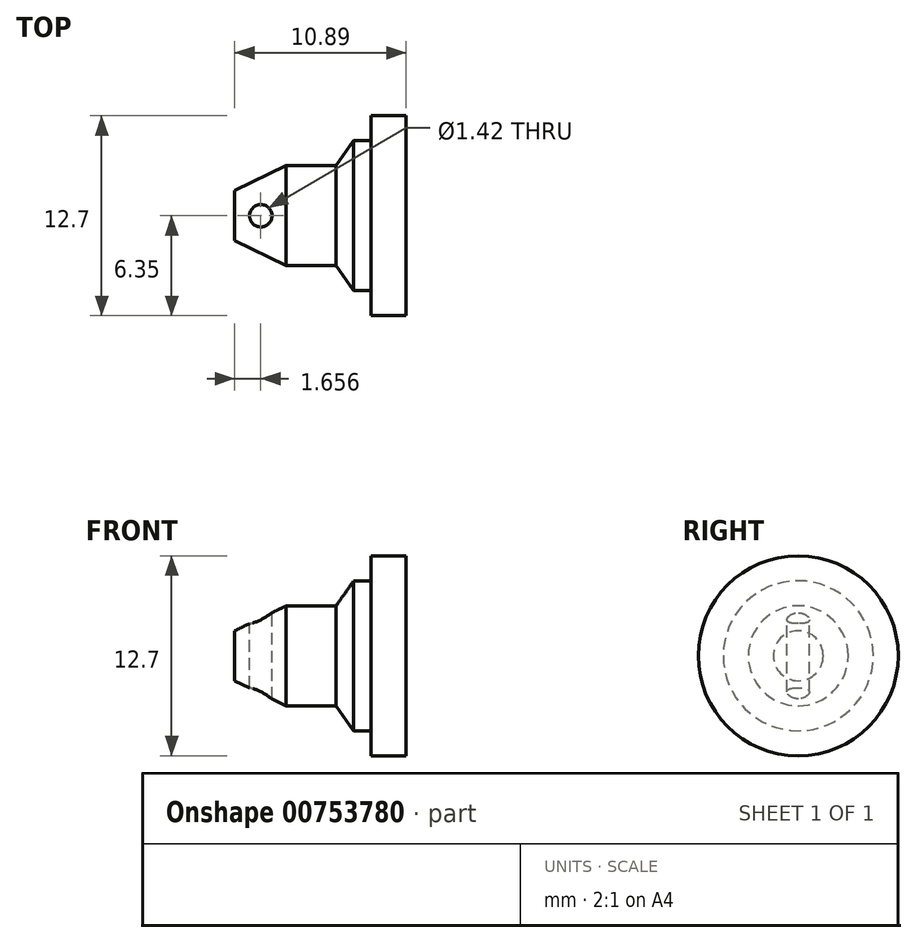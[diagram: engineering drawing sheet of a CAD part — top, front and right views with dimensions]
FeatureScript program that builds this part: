
annotation { "Feature Type Name" : "Feature", "Feature Type Description" : "" }
export const myFeature = defineFeature(function(context is Context, id is Id, definition is map)
    precondition{}
    {
        {
            var Q0;
            Q0=qCreatedBy(makeId("Top.planeOp"),FACE);
            var sketch = newSketch(context, id + "F0", { "sketchPlane" : qUnion([Q0])});
            skLineSegment(sketch, "E0", {"start": v(0, 3.18) * mm, "end": v(3.18, 3.18) * mm});
            skLineSegment(sketch, "E1", {"start": v(0, 0) * mm, "end": v(7.62, 0) * mm});
            skLineSegment(sketch, "E2", {"start": v(7.62, 0) * mm, "end": v(7.62, 6.35) * mm});
            skLineSegment(sketch, "E3", {"start": v(7.62, 6.35) * mm, "end": v(5.4, 6.35) * mm});
            skLineSegment(sketch, "E4", {"start": v(3.18, 3.18) * mm, "end": v(4.29, 4.76) * mm});
            skPoint(sketch, "E5.start.orphan", {"position": v(3.18, 6.35) * mm});
            skLineSegment(sketch, "E6", {"start": v(5.4, 6.35) * mm, "end": v(5.4, 4.76) * mm});
            skPoint(sketch, "E6.endSnap0", {"position": v(4.29, 4.76) * mm});
            skLineSegment(sketch, "E7", {"start": v(5.4, 4.76) * mm, "end": v(4.29, 4.76) * mm});
            skLineSegment(sketch, "E8", {"start": v(-3.27, 0) * mm, "end": v(-3.27, 1.59) * mm});
            skPoint(sketch, "E8.endSnap0", {"position": v(0, 1.59) * mm});
            skLineSegment(sketch, "E9", {"start": v(-3.27, 1.59) * mm, "end": v(0, 3.18) * mm});
            skLineSegment(sketch, "E10", {"start": v(-3.27, 0) * mm, "end": v(0, 0) * mm});
            skSolve(sketch);
        }
        {
            var Q0;
            Q0=makeQuery(id+"F0.imprint","IMPRINT",FACE,{"disambiguationData":[TD([[makeQuery(id+"F0.imprint","IMPRINT",EDGE,{"derivedFrom":sQuery(id+"F0.wireOp",EDGE,"E0")}),-1.0]])]});
            var Q1;
            Q1=sQuery(id+"F0.wireOp",EDGE,"E1");
            revolve(context, id + "F1", {"surfaceOperationType" : NewSurfaceOperationType.NEW, "entities" : qUnion([Q0]), "axis" : qUnion([Q1]), "revolveType" : RevolveType.FULL});
        }
        {
            var Q0;
            Q0=qCreatedBy(makeId("Top.planeOp"),FACE);
            var sketch = newSketch(context, id + "F2", { "sketchPlane" : qUnion([Q0])});
            skLineSegment(sketch, "E11", {"start": v(0, 0) * mm, "end": v(-3.23, 0) * mm});
            skCircle(sketch, "E12", {"center": v(-1.61, 0) * mm, "radius": 0.71 * mm});
            skSolve(sketch);
        }
        {
            var Q0;
            Q0 = qSketchRegion(id + "F2", true);
            extrude(context, id + "F3", {"entities" : qUnion([Q0]), "operationType" : NewBodyOperationType.REMOVE, "endBound" : BoundingType.THROUGH_ALL, "oppositeDirection" : true, "depth" : 25.4 * mm, "offsetDistance" : 25.4 * mm, "hasSecondDirection" : true, "secondDirectionBound" : SecondDirectionBoundingType.THROUGH_ALL, "secondDirectionOppositeDirection" : false, "secondDirectionDepth" : 25.4 * mm});
        }
    });
